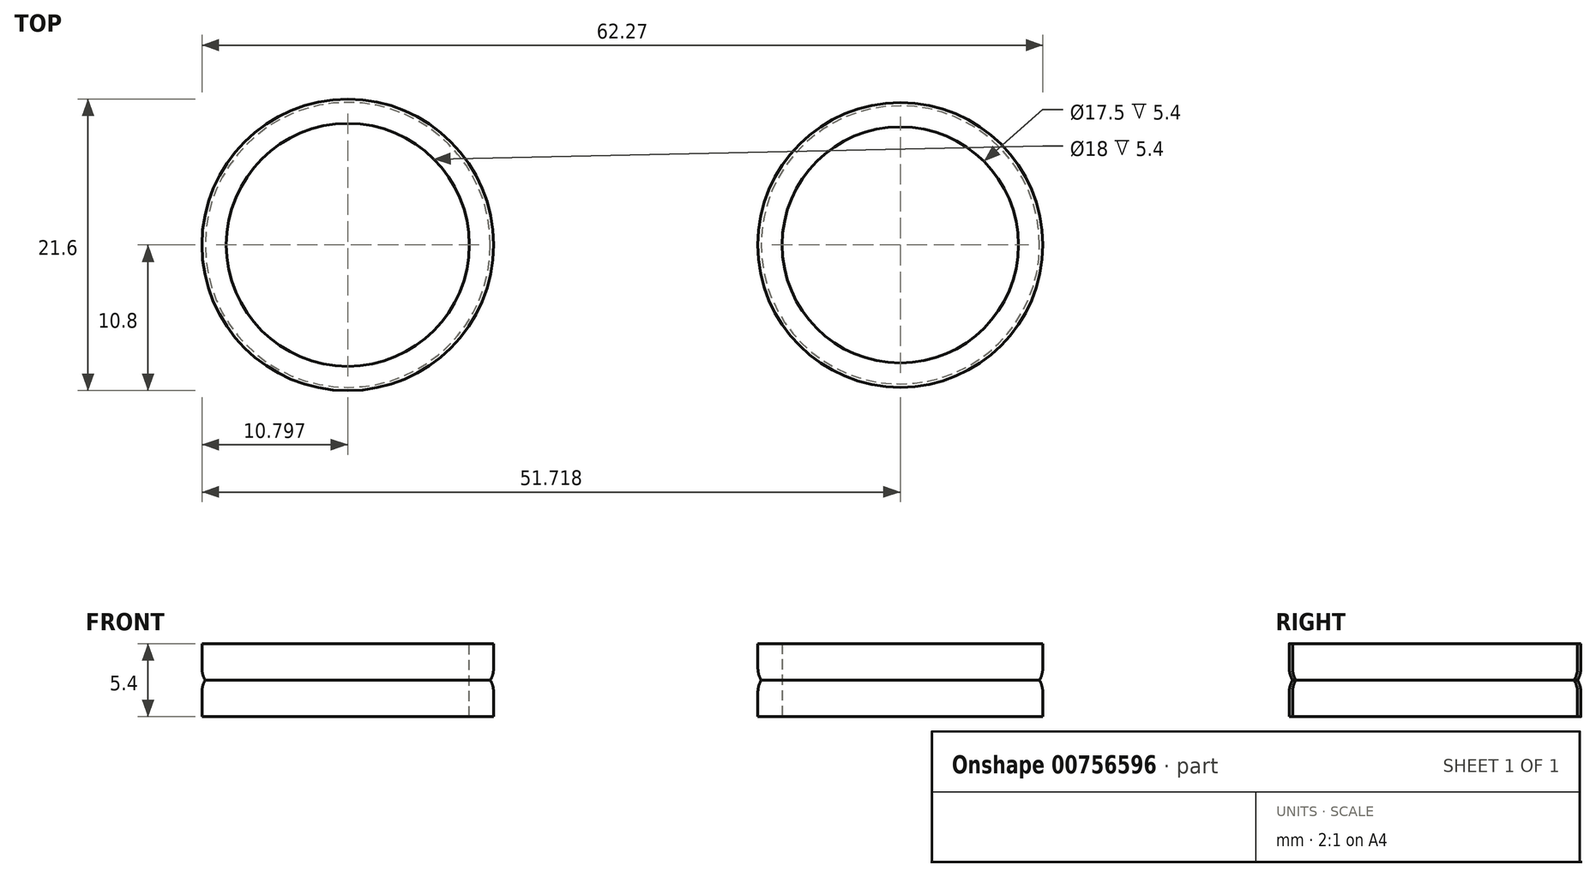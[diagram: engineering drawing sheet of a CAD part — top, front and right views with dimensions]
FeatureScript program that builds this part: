
annotation { "Feature Type Name" : "Feature", "Feature Type Description" : "" }
export const myFeature = defineFeature(function(context is Context, id is Id, definition is map)
    precondition{}
    {
        {
            var Q0;
            Q0=qCreatedBy(makeId("Front.planeOp"),FACE);
            var sketch = newSketch(context, id + "F0", { "sketchPlane" : qUnion([Q0])});
            skLineSegment(sketch, "E0", {"start": v(11, 0) * mm, "end": v(11, 5.4) * mm});
            skLineSegment(sketch, "E1", {"start": v(11, 2.7) * mm, "end": v(2, 2.7) * mm});
            skLineSegment(sketch, "E2", {"start": v(2, 2.7) * mm, "end": v(2, 4.93) * mm});
            skLineSegment(sketch, "E3", {"start": v(2, 4.93) * mm, "end": v(2, 0) * mm});
            skLineSegment(sketch, "E4", {"start": v(11, 2.7) * mm, "end": v(11.8, 2.7) * mm});
            skLineSegment(sketch, "E5", {"start": v(11, 5.4) * mm, "end": v(11, 3.6) * mm});
            skLineSegment(sketch, "E6", {"start": v(11, 3.6) * mm, "end": v(11, 1.8) * mm});
            skArc(sketch, "E7", {"start": v(11, 0) * mm, "mid": v(12.6, 0.96) * mm, "end": v(12.49, 2.82) * mm});
            skArc(sketch, "E8", {"start": v(11, 1.8) * mm, "mid": v(12.28, 2.33) * mm, "end": v(12.8, 3.6) * mm});
            skArc(sketch, "E9", {"start": v(11, 0) * mm, "mid": v(12.8, 1.8) * mm, "end": v(11, 3.6) * mm});
            skLineSegment(sketch, "E10.bottom", {"start": v(11, 5.4) * mm, "end": v(12.8, 5.4) * mm});
            skLineSegment(sketch, "E10.top", {"start": v(11, 0) * mm, "end": v(12.8, 0) * mm});
            skLineSegment(sketch, "E10.left", {"start": v(11, 5.4) * mm, "end": v(11, 0) * mm});
            skLineSegment(sketch, "E10.right", {"start": v(12.8, 5.4) * mm, "end": v(12.8, 3.6) * mm});
            skLineSegment(sketch, "E11.trimOffspring", {"start": v(12.8, 1.8) * mm, "end": v(12.8, 0) * mm});
            skSolve(sketch);
        }
        {
            var Q0;
            {var subQ6=sQuery(id+"F0.wireOp",EDGE,"E10.bottom");Q0=makeQuery(id+"F0.imprint","IMPRINT",FACE,{"disambiguationData":[TD([[makeQuery(id+"F0.imprint","IMPRINT",EDGE,{"derivedFrom":subQ6}),-1.0]])]});}
            var Q1;
            {var subQ2=sQuery(id+"F0.wireOp",EDGE,"E9");var subQ4=makeQuery(id+"F0.imprint","IMPRINT",VERTEX,{"derivedFrom":subQ2});Q1=makeQuery(id+"F0.imprint","IMPRINT",FACE,{"disambiguationData":[TD([[makeQuery(id+"F0.imprint","IMPRINT",EDGE,{"disambiguationData":[TD([[subQ4,1.0]])],"derivedFrom":subQ2}),1.0]])]});}
            var Q2;
            {var subQ0=sQuery(id+"F0.wireOp",EDGE,"E10.left");var subQ1=sQuery(id+"F0.wireOp",EDGE,"E8");var subQ2=makeQuery(id+"F0.imprint","INTERSECT",VERTEX,{"derivedFrom":[subQ1,subQ0]});Q2=makeQuery(id+"F0.imprint","IMPRINT",FACE,{"disambiguationData":[TD([[makeQuery(id+"F0.imprint","IMPRINT",EDGE,{"disambiguationData":[TD([[subQ2,-1.0]])],"derivedFrom":subQ1}),-1.0]])]});}
            var Q3;
            {var subQ0=sQuery(id+"F0.wireOp",EDGE,"E10.top");Q3=makeQuery(id+"F0.imprint","IMPRINT",FACE,{"disambiguationData":[TD([[makeQuery(id+"F0.imprint","IMPRINT",EDGE,{"derivedFrom":subQ0}),1.0]])]});}
            var Q4;
            Q4=sQuery(id+"F0.wireOp",EDGE,"E3");
            revolve(context, id + "F1", {"surfaceOperationType" : NewSurfaceOperationType.NEW, "entities" : qUnion([Q0, Q1, Q2, Q3]), "axis" : qUnion([Q4]), "revolveType" : RevolveType.FULL});
        }
        {
            var Q0;
            Q0=qCreatedBy(makeId("Front.planeOp"),FACE);
            var sketch = newSketch(context, id + "F2", { "sketchPlane" : qUnion([Q0])});
            skLineSegment(sketch, "E12", {"start": v(51.68, 5.4) * mm, "end": v(51.68, 0) * mm});
            skLineSegment(sketch, "E13", {"start": v(51.68, 0) * mm, "end": v(51.68, 1.8) * mm});
            skLineSegment(sketch, "E14", {"start": v(51.68, 1.8) * mm, "end": v(51.68, 3.6) * mm});
            skLineSegment(sketch, "E15", {"start": v(51.68, 3.6) * mm, "end": v(42.93, 3.6) * mm});
            skArc(sketch, "E16", {"start": v(51.68, 1.8) * mm, "mid": v(52.95, 2.33) * mm, "end": v(53.48, 3.6) * mm});
            skArc(sketch, "E17", {"start": v(53.48, 1.8) * mm, "mid": v(52.95, 3.07) * mm, "end": v(51.68, 3.6) * mm});
            skLineSegment(sketch, "E18.bottom", {"start": v(51.68, 5.4) * mm, "end": v(53.48, 5.4) * mm});
            skLineSegment(sketch, "E18.top", {"start": v(51.68, 0) * mm, "end": v(53.48, 0) * mm});
            skLineSegment(sketch, "E18.right", {"start": v(53.48, 5.4) * mm, "end": v(53.48, 3.6) * mm});
            skLineSegment(sketch, "E19.trimOffspring", {"start": v(53.48, 1.8) * mm, "end": v(53.48, 0) * mm});
            skLineSegment(sketch, "E20", {"start": v(42.93, 3.6) * mm, "end": v(42.93, 7.73) * mm});
            skSolve(sketch);
        }
        {
            var Q0;
            {var subQ0=sQuery(id+"F2.wireOp",EDGE,"E18.bottom");Q0=makeQuery(id+"F2.imprint","IMPRINT",FACE,{"disambiguationData":[TD([[makeQuery(id+"F2.imprint","IMPRINT",EDGE,{"derivedFrom":subQ0}),-1.0]])]});}
            var Q1;
            {var subQ0=sQuery(id+"F2.wireOp",EDGE,"E12");var subQ1=sQuery(id+"F2.wireOp",EDGE,"E16");var subQ2=makeQuery(id+"F2.imprint","INTERSECT",VERTEX,{"derivedFrom":[subQ1,subQ0]});Q1=makeQuery(id+"F2.imprint","IMPRINT",FACE,{"disambiguationData":[TD([[makeQuery(id+"F2.imprint","IMPRINT",EDGE,{"disambiguationData":[TD([[subQ2,-1.0]])],"derivedFrom":subQ1}),1.0]])]});}
            var Q2;
            {var subQ3=sQuery(id+"F2.wireOp",EDGE,"E18.top");Q2=makeQuery(id+"F2.imprint","IMPRINT",FACE,{"disambiguationData":[TD([[makeQuery(id+"F2.imprint","IMPRINT",EDGE,{"derivedFrom":subQ3}),1.0]])]});}
            var Q3;
            Q3=sQuery(id+"F2.wireOp",EDGE,"E20");
            revolve(context, id + "F3", {"surfaceOperationType" : NewSurfaceOperationType.NEW, "entities" : qUnion([Q0, Q1, Q2]), "axis" : qUnion([Q3]), "revolveType" : RevolveType.FULL});
        }
    });
